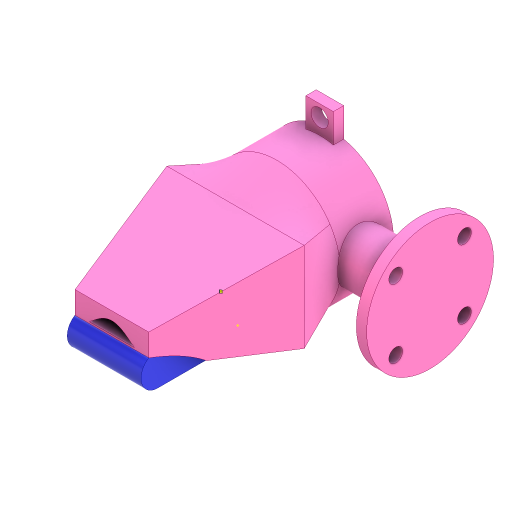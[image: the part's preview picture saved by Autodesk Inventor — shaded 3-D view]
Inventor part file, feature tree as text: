
AUTODESK INVENTOR PART (.ipt)
format: ipt  version: 2024 (Build 280153000, 153)  size: 1,493,504 bytes
history: native  units: mm
features: sketch x24, extrude x23, split x10, projected_geometry x10, other x9, boolean_combine x6, plane x5, loft x5, fillet x2, thicken_offset x2, sweep x1
ambient origin geometry x8: Origin, YZ Plane, XZ Plane, XY Plane, X Axis, Y Axis, Z Axis, Center Point
bodies: Solid1 (feature_tree), Solid2 (feature_tree), Solid19 (feature_tree), Solid21 (feature_tree), Solid22 (feature_tree), Solid23 (feature_tree), Solid24 (feature_tree), Solid3 (feature_tree), Solid4 (feature_tree), Solid5 (feature_tree), Solid6 (feature_tree), Solid7 (feature_tree), Solid8 (feature_tree), Solid9 (feature_tree), Solid10 (feature_tree), Solid11 (feature_tree), Solid12 (feature_tree), Solid13 (feature_tree), Solid14 (feature_tree), Solid15 (feature_tree), Solid16 (feature_tree), Solid17 (feature_tree), Solid18 (feature_tree)
feature tree (97):
  extrude  "Extrusion1"  Depth=9.5mm TaperAngle=0.0deg
  extrude  "Extrusion2"  Depth=3.0mm TaperAngle=0.0deg
  extrude  "Extrusion3"  Depth=40.0mm
  plane  "Work Plane2"
  sketch  "Sketch4"  dims[d4=29.0mm d5=3.0mm d6=0.0mm]
  loft  "Loft1"
  loft  "Loft2"
  loft  "Loft3"
  loft  "Loft4"
  boolean_combine  "Combine1"
  loft  "Loft5"
  fillet  "Fillet1"  [1 undecoded]
  fillet  "Fillet2"  [1 undecoded]
  plane  "Work Plane3"
  extrude  "Extrusion5"  TaperAngle=0.0deg  [1 undecoded]
  extrude  "Extrusion6"  TaperAngle=0.0deg  [1 undecoded]
  extrude  "Extrusion7"  Depth=40.0mm
  extrude  "Extrusion8"  TaperAngle=0.0deg  [1 undecoded]
  extrude  "Extrusion9"  Depth=2.0mm
  extrude  "Extrusion10"  Depth=38.0mm
  extrude  "Extrusion11"  Depth=3.0mm TaperAngle=0.0deg
  extrude  "Extrusion12"  Depth=3.0mm TaperAngle=0.0deg
  extrude  "Extrusion14"  Depth=12.5mm TaperAngle=0.0deg
  extrude  "Extrusion15"  Depth=3.7mm TaperAngle=0.0deg
  split  "Split1"
  split  "Split2"
  split  "Split3"
  split  "Split4"
  split  "Split5"
  split  "Split6"
  split  "Split7"
  boolean_combine  "Combine2"
  split  "Split8"
  boolean_combine  "Combine3"
  boolean_combine  "Combine4"
  extrude  "Extrusion16"  Depth=8.5mm
  extrude  "Extrusion17"  Depth=8.5mm
  sketch  "Sketch36"  dims[d43=1.5mm d46=38.0mm]
  sweep  "Sweep1"
  split  "Split9"
  thicken_offset  "Thicken1"
  extrude  "Extrusion18"  Depth=10.0mm
  split  "Split10"
  thicken_offset  "Thicken2"
  boolean_combine  "Combine5"
  plane  "Work Plane4"
  extrude  "Extrusion19"  Depth=2.5mm TaperAngle=0.0deg
  other  "Work Point1"
  other  "Work Point3"
  extrude  "Extrusion20"  Depth=2.5mm TaperAngle=0.0deg
  extrude  "Extrusion21"  Depth=5.5mm
  extrude  "Extrusion22"  Depth=8.5mm
  extrude  "Extrusion23"  Depth=8.5mm
  extrude  "Extrusion24"  Depth=2.5mm TaperAngle=0.0deg
  boolean_combine  "Combine6"
  plane  "Work Plane5"
  extrude  "Extrusion25"  Depth=2.5mm TaperAngle=0.0deg
  sketch  "Sketch1"  dims[d0=3.0mm d1=0.0mm d2=9.5mm d3=0.0mm]
  plane  "Work Plane1"
  other  "2D Equation Curve1"
  other  "Edges1"
  other  "Edges2"
  other  "Edges3"
  other  "Edges4"
  sketch  "Sketch7"  dims[d7=12.0mm d8=36.0mm d9=40.0mm]
  sketch  "Sketch10"  dims[d10=9.0mm d11=10.0mm]
  sketch  "Sketch12"  dims[d12=3.0mm d13=-6.5mm d14=6.5mm]
  sketch  "Sketch13"  dims[d15=40.0mm d16=26.0mm]
  sketch  "Sketch16"  dims[d17=20.0mm d18=20.0mm]
  projected_geometry  "Projected Loop1"
  sketch  "Sketch19"  dims[d19=0.0mm d20=90.0deg d21=0.0mm d22=90.0deg d23=0.0mm d24=90.0deg d25=0.0mm d26=90.0deg]
  projected_geometry  "Projected Loop2"
  projected_geometry  "Projected Loop3"
  projected_geometry  "Projected Loop4"
  projected_geometry  "Projected Loop5"
  sketch  "Sketch23"  dims[d27=0.0mm d28=90.0deg d29=0.0mm d30=90.0deg]
  sketch  "Sketch24"  dims[d31=0.0mm d32=90.0deg d33=0.0mm d34=90.0deg]
  sketch  "Sketch28"  dims[d35=26.0mm d36=40.0mm]
  sketch  "Sketch29"  dims[d37=4.0mm d38=0.0mm d39=90.0deg]
  sketch  "Sketch35"  dims[d40=0.0mm d41=90.0deg d42=2.0mm]
  projected_geometry  "Projected Loop11"
  sketch  "3D Sketch2"
  other  "Srf1"
  sketch  "Sketch38"  dims[d47=15.0mm d48=3.0mm d49=0.0mm]
  projected_geometry  "Projected Loop12"
  sketch  "Sketch47"  dims[d50=15.0mm d51=3.0mm d52=0.0mm]
  projected_geometry  "Projected Loop22"
  sketch  "Sketch49"  dims[d53=11.0mm d54=12.5mm d55=0.0mm]
  sketch  "Sketch50"  dims[d56=11.0mm d57=3.7mm d58=0.0mm]
  sketch  "Sketch52"  dims[d59=20.0mm d60=0.0mm d61=8.5mm]
  sketch  "Sketch53"  dims[d62=8.5mm d63=8.5mm]
  projected_geometry  "Projected Loop25"
  projected_geometry  "Projected Loop26"
  sketch  "Sketch54"  dims[d64=8.5mm d65=2.7mm d66=0.0mm]
  sketch  "Sketch56"  dims[d67=40.0mm d68=10.0mm]
  sketch  "Sketch58"  dims[d69=2.7mm d70=0.0mm d71=2.5mm d72=0.0mm d73=2.5mm d74=0.0mm d80=5.5mm d81=8.5mm d82=8.5mm d83=2.5mm d84=0.0mm d85=2.5mm d86=0.0mm d87=0.5mm d88=0.0mm d89=0.0mm d91=10.0mm d92=10.0mm d93=0.1mm d94=0.0mm d95=16.5mm d96=2.5mm d97=4.0mm d98=2.5mm d99=2.5mm d100=5.0mm d101=5.0mm d102=2.5mm d103=2.5mm d104=2.5mm d105=2.5mm d106=0.0mm d107=0.0mm d108=2.5mm d109=2.5mm d114=0.1mm d115=0.1mm d116=0.1mm d117=0.0mm d130=0.1mm d131=0.1mm d132=58.25mm d133=6.0mm d134=16.0mm d135=0.0mm d136=12.0mm d137=12.0mm d138=12.0mm d139=12.0mm d140=10.0mm d141=0.0mm d142=0.0mm d143=0.0mm d144=0.0mm d145=0.0mm d146=0.0mm d147=0.0mm d148=9.273806mm d149=9.273806mm d150=0.0mm d151=0.0mm d152=21.5mm d153=0.0mm d110=0.5mm d111=0.872665mm d112=0.5mm d113=0.872665mm]
  other  "Unwrap1"
note: 5 required parameter values undecoded (feature->parameter linkage not recoverable at this tier; creation-order binding heuristic only, values carry confidence <= 0.55)
